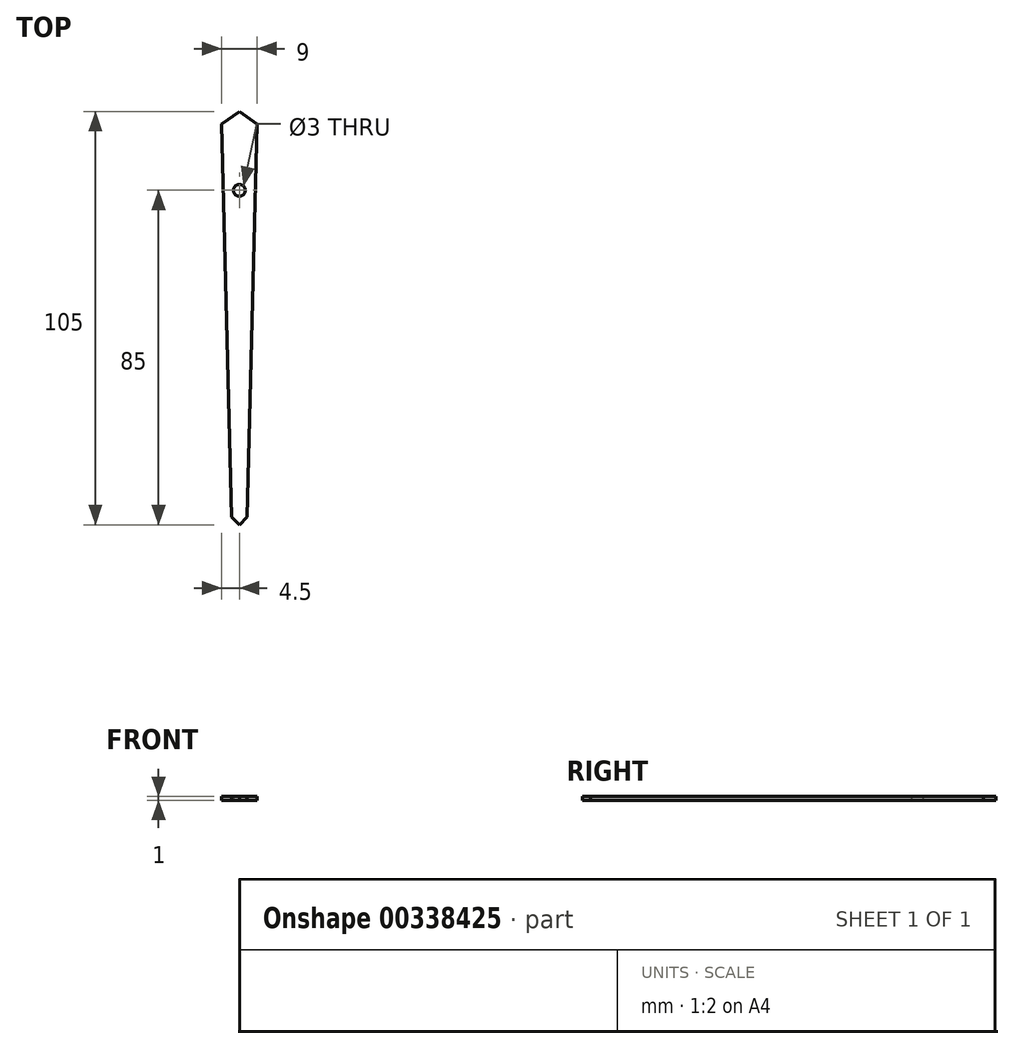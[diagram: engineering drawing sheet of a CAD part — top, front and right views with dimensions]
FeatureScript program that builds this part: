
annotation { "Feature Type Name" : "Feature", "Feature Type Description" : "" }
export const myFeature = defineFeature(function(context is Context, id is Id, definition is map)
    precondition{}
    {
        {
            var Q0;
            Q0=qCreatedBy(makeId("Top.planeOp"),FACE);
            var sketch = newSketch(context, id + "F0", { "sketchPlane" : qUnion([Q0])});
            skCircle(sketch, "E0", {"center": v(0, 0) * mm, "radius": 105 * mm, "construction": true});
            skLineSegment(sketch, "E1", {"start": v(0, 20) * mm, "end": v(0, -85) * mm, "construction": true});
            skLineSegment(sketch, "E2", {"start": v(0, -85) * mm, "end": v(2, -83) * mm});
            skLineSegment(sketch, "E3", {"start": v(0, -85) * mm, "end": v(-2, -83) * mm});
            skLineSegment(sketch, "E4", {"start": v(-2, -83) * mm, "end": v(-4.5, 16.85) * mm});
            skLineSegment(sketch, "E5", {"start": v(-4.5, 16.85) * mm, "end": v(0, 20) * mm});
            skLineSegment(sketch, "E6", {"start": v(0, 20) * mm, "end": v(4.5, 16.85) * mm});
            skLineSegment(sketch, "E7", {"start": v(4.5, 16.85) * mm, "end": v(2, -83) * mm});
            skCircle(sketch, "E8", {"center": v(0, 0) * mm, "radius": 1.5 * mm});
            skCircle(sketch, "E9", {"center": v(0, 0) * mm, "radius": 125 * mm, "construction": true});
            skSolve(sketch);
        }
        {
            var Q0;
            Q0=makeQuery(id+"F0.imprint","IMPRINT",FACE,{"disambiguationData":[TD([[makeQuery(id+"F0.imprint","IMPRINT",EDGE,{"derivedFrom":sQuery(id+"F0.wireOp",EDGE,"E2")}),1.0]])]});
            extrude(context, id + "F1", {"entities" : qUnion([Q0]), "depth" : 1 * mm});
        }
    });
